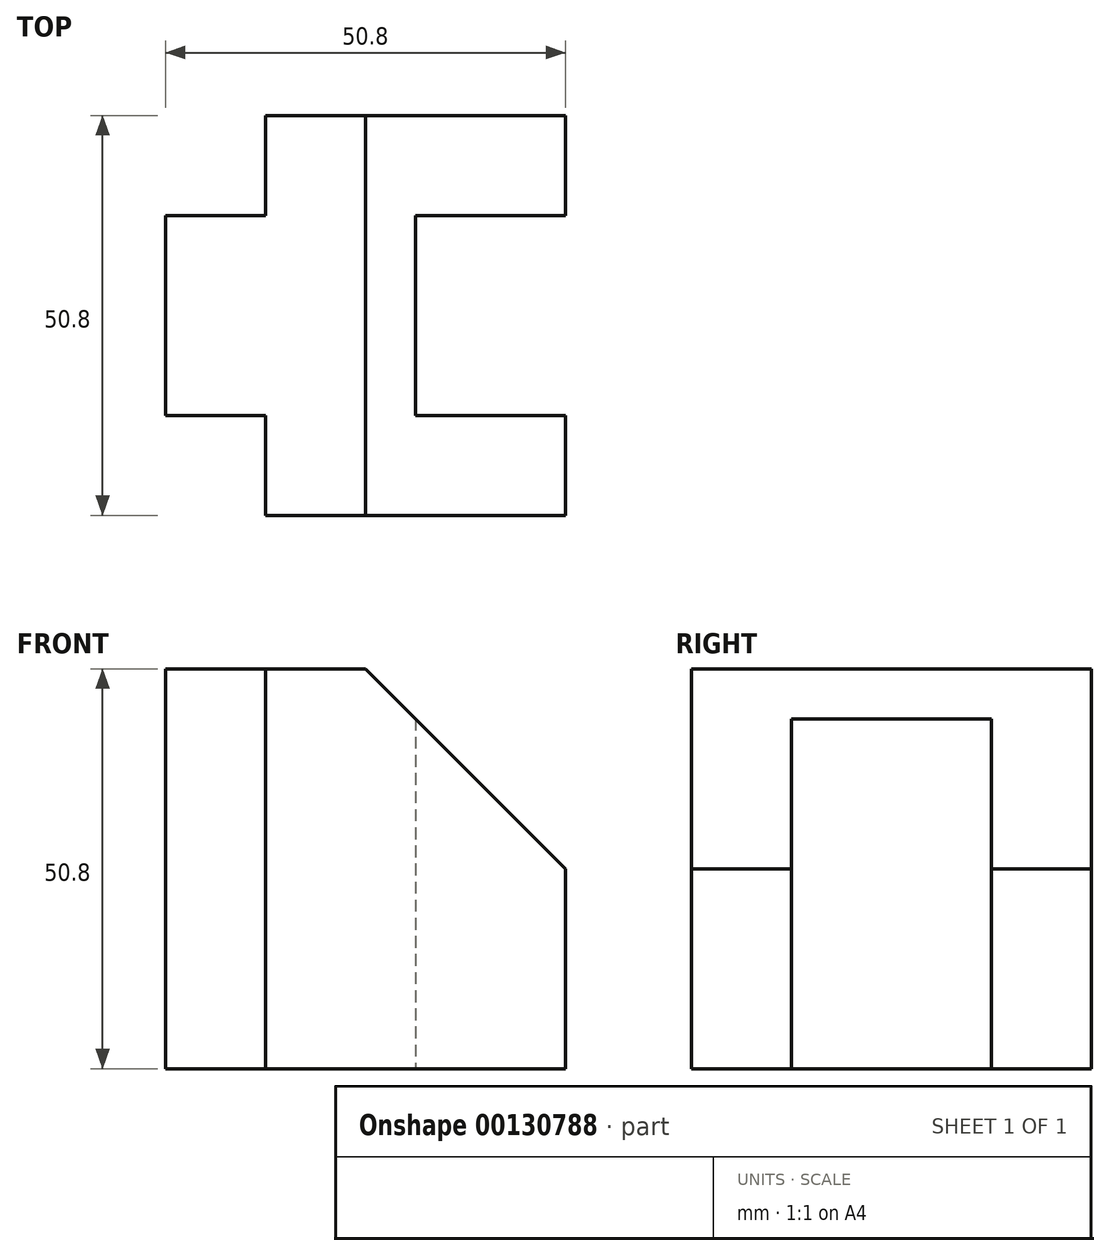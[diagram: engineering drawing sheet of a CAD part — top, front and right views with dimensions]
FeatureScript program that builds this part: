
annotation { "Feature Type Name" : "Feature", "Feature Type Description" : "" }
export const myFeature = defineFeature(function(context is Context, id is Id, definition is map)
    precondition{}
    {
        {
            var Q0;
            Q0=qCreatedBy(makeId("Top.planeOp"),FACE);
            var sketch = newSketch(context, id + "F0", { "sketchPlane" : qUnion([Q0])});
            skLineSegment(sketch, "E0", {"start": v(38.1, 0) * mm, "end": v(38.1, 12.7) * mm});
            skLineSegment(sketch, "E1", {"start": v(38.1, 12.7) * mm, "end": v(19.05, 12.7) * mm});
            skLineSegment(sketch, "E2", {"start": v(19.05, 12.7) * mm, "end": v(19.05, 38.1) * mm});
            skLineSegment(sketch, "E3", {"start": v(19.05, 38.1) * mm, "end": v(38.1, 38.1) * mm});
            skLineSegment(sketch, "E4", {"start": v(38.1, 38.1) * mm, "end": v(38.1, 50.8) * mm});
            skLineSegment(sketch, "E5", {"start": v(38.1, 50.8) * mm, "end": v(0, 50.8) * mm});
            skLineSegment(sketch, "E6", {"start": v(0, 50.8) * mm, "end": v(0, 38.1) * mm});
            skLineSegment(sketch, "E7", {"start": v(0, 38.1) * mm, "end": v(-12.7, 38.1) * mm});
            skLineSegment(sketch, "E8", {"start": v(-12.7, 38.1) * mm, "end": v(-12.7, 12.7) * mm});
            skLineSegment(sketch, "E9", {"start": v(-12.7, 12.7) * mm, "end": v(0, 12.7) * mm});
            skLineSegment(sketch, "E10", {"start": v(0, 12.7) * mm, "end": v(0, 0) * mm});
            skLineSegment(sketch, "E11", {"start": v(0, 0) * mm, "end": v(38.1, 0) * mm});
            skSolve(sketch);
        }
        {
            var Q0;
            Q0 = qSketchRegion(id + "F0", true);
            extrude(context, id + "F1", {"entities" : qUnion([Q0]), "depth" : 50.8 * mm});
        }
        {
            var Q0;
            Q0=makeQuery(id+"F1.opExtrude","SWEPT_FACE",FACE,{"disambiguationData":[OSD([sQuery(id+"F0.wireOp",EDGE,"E11")])]});
            var sketch = newSketch(context, id + "F2", { "sketchPlane" : qUnion([Q0])});
            skLineSegment(sketch, "E12", {"start": v(12.7, 50.8) * mm, "end": v(38.1, 25.4) * mm});
            skLineSegment(sketch, "E13", {"start": v(38.1, 25.4) * mm, "end": v(38.1, 50.8) * mm});
            skLineSegment(sketch, "E14", {"start": v(38.1, 50.8) * mm, "end": v(12.7, 50.8) * mm});
            skSolve(sketch);
        }
        {
            var Q0;
            Q0=makeQuery(id+"F2.imprint","IMPRINT",FACE,{"disambiguationData":[TD([[makeQuery(id+"F2.imprint","IMPRINT",EDGE,{"derivedFrom":sQuery(id+"F2.wireOp",EDGE,"E12")}),1.0]])]});
            extrude(context, id + "F3", {"entities" : qUnion([Q0]), "operationType" : NewBodyOperationType.REMOVE, "endBound" : BoundingType.THROUGH_ALL, "oppositeDirection" : true, "depth" : 25.4 * mm});
        }
    });
